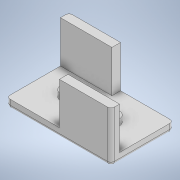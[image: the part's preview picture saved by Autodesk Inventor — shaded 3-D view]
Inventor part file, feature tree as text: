
AUTODESK INVENTOR PART (.ipt)
format: ipt  version: 2020 (Build 240168000, 168)  size: 168,448 bytes
history: native  units: in
note: dims shown in document units (in); Inventor stores cm internally (conversion verified against a paired STEP export)
features: extrude x5, sketch x5, chamfer x1, fillet x1
ambient origin geometry x8: Origin, YZ Plane, XZ Plane, XY Plane, X Axis, Y Axis, Z Axis, Center Point
bodies: Solid1 (feature_tree)
feature tree (12):
  extrude  "Extrusion1"  Depth=1.4331in
  extrude  "Extrusion2"  Depth=1.1811in
  extrude  "Extrusion3"  Depth=1.1811in
  extrude  "Extrusion4"  Depth=0.9606in TaperAngle=0.0deg
  extrude  "Extrusion5"  Depth=0.0787in
  chamfer  "Chamfer1"  Distance=0.1969in
  fillet  "Fillet1"  Radius=0.1575in
  sketch  "Sketch1"  dims[d0=2.3937in d1=1.4331in]
  sketch  "Sketch2"  dims[d2=0.1969in d3=0.0in d4=1.1811in]
  sketch  "Sketch3"  dims[d5=0.1969in d6=1.1811in]
  sketch  "Sketch4"  dims[d7=0.1969in d8=0.9606in d9=0.0in]
  sketch  "Sketch5"  dims[d10=0.3406in d11=0.3406in d12=0.1969in d13=0.0in d14=0.1575in d15=0.1575in d16=0.5906in d17=0.0in d18=0.2362in d19=0.2362in d20=0.1181in d21=0.0in d22=0.0591in d23=0.0787in d24=45.0deg d25=0.0787in]
